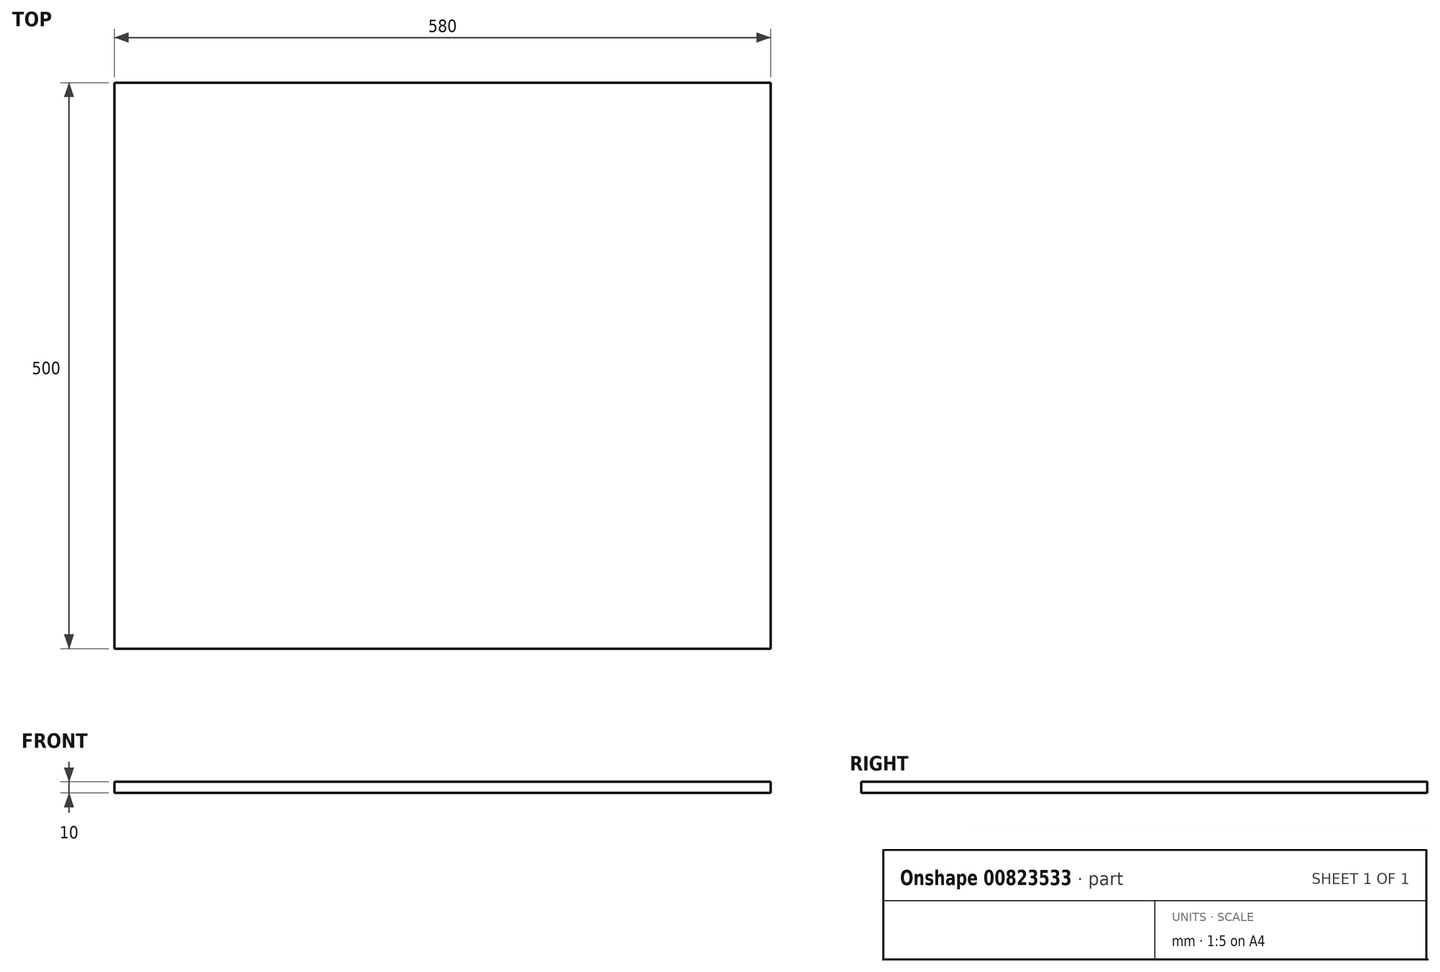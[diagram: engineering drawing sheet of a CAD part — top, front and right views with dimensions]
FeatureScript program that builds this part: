
annotation { "Feature Type Name" : "Feature", "Feature Type Description" : "" }
export const myFeature = defineFeature(function(context is Context, id is Id, definition is map)
    precondition{}
    {
        {
            var Q0;
            Q0=qCreatedBy(makeId("Top.planeOp"),FACE);
            var sketch = newSketch(context, id + "F0", { "sketchPlane" : qUnion([Q0])});
            skLineSegment(sketch, "E0.bottom", {"start": v(290, -250) * mm, "end": v(-290, -250) * mm});
            skLineSegment(sketch, "E0.top", {"start": v(290, 250) * mm, "end": v(-290, 250) * mm});
            skLineSegment(sketch, "E0.left", {"start": v(290, -250) * mm, "end": v(290, 250) * mm});
            skLineSegment(sketch, "E0.right", {"start": v(-290, -250) * mm, "end": v(-290, 250) * mm});
            skPoint(sketch, "E0.middle", {"position": v(0, 0) * mm});
            skSolve(sketch);
        }
        {
            var Q0;
            Q0 = qSketchRegion(id + "F0", true);
            extrude(context, id + "F1", {"entities" : qUnion([Q0]), "depth" : 10 * mm, "offsetDistance" : 25 * mm});
        }
    });
